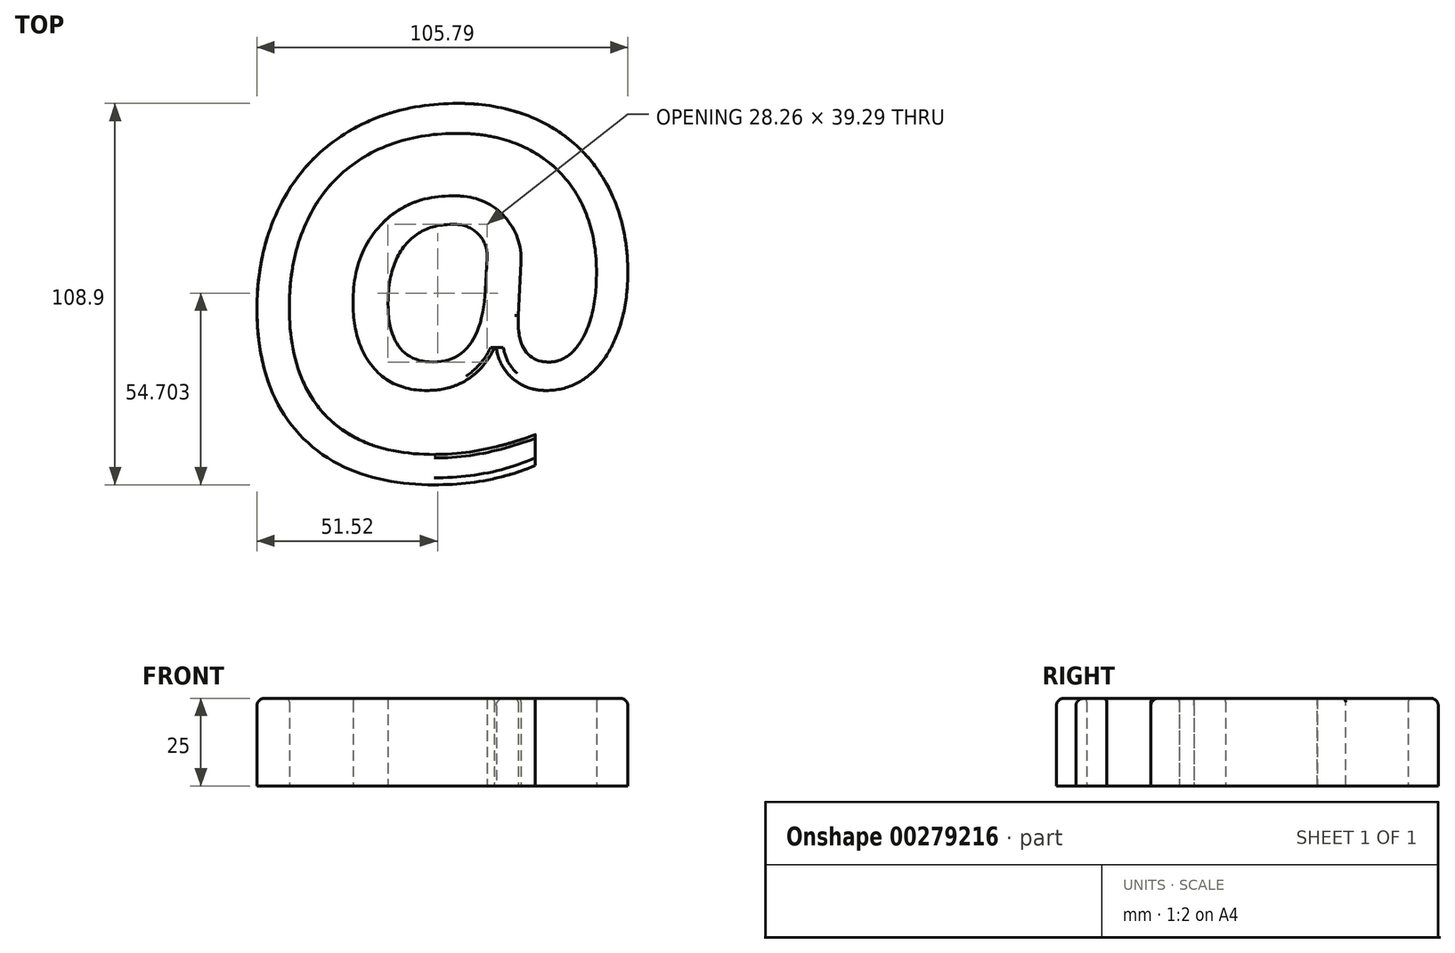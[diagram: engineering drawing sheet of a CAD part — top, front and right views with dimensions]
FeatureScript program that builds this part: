
annotation { "Feature Type Name" : "Feature", "Feature Type Description" : "" }
export const myFeature = defineFeature(function(context is Context, id is Id, definition is map)
    precondition{}
    {
        {
            var Q0;
            Q0=qCreatedBy(makeId("Top.planeOp"),FACE);
            var sketch = newSketch(context, id + "F0", { "sketchPlane" : qUnion([Q0])});
            skText(sketch, "E0", { "text": "@", "fontName": "OpenSans-Regular.ttf"});
            const initialGuessF0  = {"E0": [0, 0, 1, 0, 0.09755]};
            skSetInitialGuess(sketch, initialGuessF0);
            skSolve(sketch);
        }
        {
            var Q0;
            Q0 = qSketchRegion(id + "F0", true);
            extrude(context, id + "F1", {"entities" : qUnion([Q0]), "depth" : 25 * mm});
        }
        {
            var Q0;
            Q0=makeQuery(id+"F1.opExtrude","SWEPT_EDGE",EDGE,{"disambiguationData":[OSD([sQuery(id+"F0.wireOp",EDGE,"E0.sketch_text.stroke-40"),sQuery(id+"F0.wireOp",EDGE,"E0.sketch_text.stroke-41")])]});
            fillet(context, id + "F2", {"entities" : qUnion([Q0]), "radius" : 9 * mm, "tangentPropagation" : true, "allowEdgeOverflow" : false});
        }
        {
            var Q0;
            Q0=makeQuery(id+"F1.opExtrude","SWEPT_EDGE",EDGE,{"disambiguationData":[OSD([sQuery(id+"F0.wireOp",EDGE,"E0.sketch_text.stroke-13"),sQuery(id+"F0.wireOp",EDGE,"E0.sketch_text.stroke-14")])]});
            fillet(context, id + "F3", {"entities" : qUnion([Q0]), "radius" : 18 * mm, "tangentPropagation" : true, "allowEdgeOverflow" : false});
        }
        {
            var Q0;
            Q0=makeQuery(id+"F1.opExtrude","CAP_EDGE",EDGE,{"disambiguationData":[OSD([sQuery(id+"F0.wireOp",EDGE,"E0.sketch_text.stroke-36")])],"isStart":false});
            fillet(context, id + "F4", {"entities" : qUnion([Q0]), "radius" : 2 * mm, "tangentPropagation" : true, "allowEdgeOverflow" : false});
        }
        {
            var Q0;
            {var subQ0=sQuery(id+"F0.wireOp",EDGE,"E0.sketch_text.stroke-14");var subQ1=sQuery(id+"F0.wireOp",EDGE,"E0.sketch_text.stroke-13");Q0=makeQuery(id+"F3.opFillet","BLEND_EDGE",EDGE,{"blendedFrom":[makeQuery(id+"F1.opExtrude","SWEPT_EDGE",EDGE,{"disambiguationData":[OSD([subQ1,subQ0])]}),makeQuery(id+"F1.opExtrude","CAP_FACE",FACE,{"disambiguationData":[OSD([sQuery(id+"F0.wireOp",EDGE,"E0.sketch_text.stroke-0"),sQuery(id+"F0.wireOp",EDGE,"E0.sketch_text.stroke-1"),sQuery(id+"F0.wireOp",EDGE,"E0.sketch_text.stroke-2"),sQuery(id+"F0.wireOp",EDGE,"E0.sketch_text.stroke-3"),sQuery(id+"F0.wireOp",EDGE,"E0.sketch_text.stroke-4"),sQuery(id+"F0.wireOp",EDGE,"E0.sketch_text.stroke-5"),sQuery(id+"F0.wireOp",EDGE,"E0.sketch_text.stroke-6"),sQuery(id+"F0.wireOp",EDGE,"E0.sketch_text.stroke-7"),sQuery(id+"F0.wireOp",EDGE,"E0.sketch_text.stroke-8"),sQuery(id+"F0.wireOp",EDGE,"E0.sketch_text.stroke-9"),sQuery(id+"F0.wireOp",EDGE,"E0.sketch_text.stroke-10"),sQuery(id+"F0.wireOp",EDGE,"E0.sketch_text.stroke-11"),sQuery(id+"F0.wireOp",EDGE,"E0.sketch_text.stroke-12"),subQ1,subQ0,sQuery(id+"F0.wireOp",EDGE,"E0.sketch_text.stroke-15"),sQuery(id+"F0.wireOp",EDGE,"E0.sketch_text.stroke-16"),sQuery(id+"F0.wireOp",EDGE,"E0.sketch_text.stroke-17"),sQuery(id+"F0.wireOp",EDGE,"E0.sketch_text.stroke-18"),sQuery(id+"F0.wireOp",EDGE,"E0.sketch_text.stroke-19"),sQuery(id+"F0.wireOp",EDGE,"E0.sketch_text.stroke-20"),sQuery(id+"F0.wireOp",EDGE,"E0.sketch_text.stroke-21"),sQuery(id+"F0.wireOp",EDGE,"E0.sketch_text.stroke-22"),sQuery(id+"F0.wireOp",EDGE,"E0.sketch_text.stroke-23"),sQuery(id+"F0.wireOp",EDGE,"E0.sketch_text.stroke-24"),sQuery(id+"F0.wireOp",EDGE,"E0.sketch_text.stroke-25"),sQuery(id+"F0.wireOp",EDGE,"E0.sketch_text.stroke-26"),sQuery(id+"F0.wireOp",EDGE,"E0.sketch_text.stroke-27"),sQuery(id+"F0.wireOp",EDGE,"E0.sketch_text.stroke-28"),sQuery(id+"F0.wireOp",EDGE,"E0.sketch_text.stroke-29"),sQuery(id+"F0.wireOp",EDGE,"E0.sketch_text.stroke-30"),sQuery(id+"F0.wireOp",EDGE,"E0.sketch_text.stroke-31"),sQuery(id+"F0.wireOp",EDGE,"E0.sketch_text.stroke-32"),sQuery(id+"F0.wireOp",EDGE,"E0.sketch_text.stroke-33"),sQuery(id+"F0.wireOp",EDGE,"E0.sketch_text.stroke-34"),sQuery(id+"F0.wireOp",EDGE,"E0.sketch_text.stroke-35"),sQuery(id+"F0.wireOp",EDGE,"E0.sketch_text.stroke-36"),sQuery(id+"F0.wireOp",EDGE,"E0.sketch_text.stroke-37"),sQuery(id+"F0.wireOp",EDGE,"E0.sketch_text.stroke-38"),sQuery(id+"F0.wireOp",EDGE,"E0.sketch_text.stroke-39"),sQuery(id+"F0.wireOp",EDGE,"E0.sketch_text.stroke-40"),sQuery(id+"F0.wireOp",EDGE,"E0.sketch_text.stroke-41"),sQuery(id+"F0.wireOp",EDGE,"E0.sketch_text.stroke-42"),sQuery(id+"F0.wireOp",EDGE,"E0.sketch_text.stroke-43")])],"isStart":false})],"blendedInto":[makeQuery(id+"F1.opExtrude","CAP_FACE",FACE,{"disambiguationData":[OSD([sQuery(id+"F0.wireOp",EDGE,"E0.sketch_text.stroke-0"),sQuery(id+"F0.wireOp",EDGE,"E0.sketch_text.stroke-1"),sQuery(id+"F0.wireOp",EDGE,"E0.sketch_text.stroke-2"),sQuery(id+"F0.wireOp",EDGE,"E0.sketch_text.stroke-3"),sQuery(id+"F0.wireOp",EDGE,"E0.sketch_text.stroke-4"),sQuery(id+"F0.wireOp",EDGE,"E0.sketch_text.stroke-5"),sQuery(id+"F0.wireOp",EDGE,"E0.sketch_text.stroke-6"),sQuery(id+"F0.wireOp",EDGE,"E0.sketch_text.stroke-7"),sQuery(id+"F0.wireOp",EDGE,"E0.sketch_text.stroke-8"),sQuery(id+"F0.wireOp",EDGE,"E0.sketch_text.stroke-9"),sQuery(id+"F0.wireOp",EDGE,"E0.sketch_text.stroke-10"),sQuery(id+"F0.wireOp",EDGE,"E0.sketch_text.stroke-11"),sQuery(id+"F0.wireOp",EDGE,"E0.sketch_text.stroke-12"),subQ1,subQ0,sQuery(id+"F0.wireOp",EDGE,"E0.sketch_text.stroke-15"),sQuery(id+"F0.wireOp",EDGE,"E0.sketch_text.stroke-16"),sQuery(id+"F0.wireOp",EDGE,"E0.sketch_text.stroke-17"),sQuery(id+"F0.wireOp",EDGE,"E0.sketch_text.stroke-18"),sQuery(id+"F0.wireOp",EDGE,"E0.sketch_text.stroke-19"),sQuery(id+"F0.wireOp",EDGE,"E0.sketch_text.stroke-20"),sQuery(id+"F0.wireOp",EDGE,"E0.sketch_text.stroke-21"),sQuery(id+"F0.wireOp",EDGE,"E0.sketch_text.stroke-22"),sQuery(id+"F0.wireOp",EDGE,"E0.sketch_text.stroke-23"),sQuery(id+"F0.wireOp",EDGE,"E0.sketch_text.stroke-24"),sQuery(id+"F0.wireOp",EDGE,"E0.sketch_text.stroke-25"),sQuery(id+"F0.wireOp",EDGE,"E0.sketch_text.stroke-26"),sQuery(id+"F0.wireOp",EDGE,"E0.sketch_text.stroke-27"),sQuery(id+"F0.wireOp",EDGE,"E0.sketch_text.stroke-28"),sQuery(id+"F0.wireOp",EDGE,"E0.sketch_text.stroke-29"),sQuery(id+"F0.wireOp",EDGE,"E0.sketch_text.stroke-30"),sQuery(id+"F0.wireOp",EDGE,"E0.sketch_text.stroke-31"),sQuery(id+"F0.wireOp",EDGE,"E0.sketch_text.stroke-32"),sQuery(id+"F0.wireOp",EDGE,"E0.sketch_text.stroke-33"),sQuery(id+"F0.wireOp",EDGE,"E0.sketch_text.stroke-34"),sQuery(id+"F0.wireOp",EDGE,"E0.sketch_text.stroke-35"),sQuery(id+"F0.wireOp",EDGE,"E0.sketch_text.stroke-36"),sQuery(id+"F0.wireOp",EDGE,"E0.sketch_text.stroke-37"),sQuery(id+"F0.wireOp",EDGE,"E0.sketch_text.stroke-38"),sQuery(id+"F0.wireOp",EDGE,"E0.sketch_text.stroke-39"),sQuery(id+"F0.wireOp",EDGE,"E0.sketch_text.stroke-40"),sQuery(id+"F0.wireOp",EDGE,"E0.sketch_text.stroke-41"),sQuery(id+"F0.wireOp",EDGE,"E0.sketch_text.stroke-42"),sQuery(id+"F0.wireOp",EDGE,"E0.sketch_text.stroke-43")])],"isStart":false})]});}
            var Q1;
            Q1=makeQuery(id+"F1.opExtrude","CAP_EDGE",EDGE,{"disambiguationData":[OSD([sQuery(id+"F0.wireOp",EDGE,"E0.sketch_text.stroke-26")])],"isStart":false});
            fillet(context, id + "F5", {"entities" : qUnion([Q0, Q1]), "radius" : 1 * mm, "tangentPropagation" : true, "allowEdgeOverflow" : false});
        }
    });
